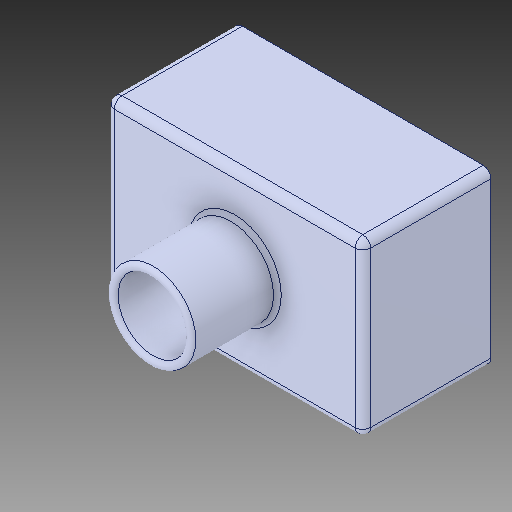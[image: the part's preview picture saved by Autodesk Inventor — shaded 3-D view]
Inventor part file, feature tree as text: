
AUTODESK INVENTOR PART (.ipt)
format: ipt  version: 2018 (Build 220112000, 112)  size: 159,232 bytes
history: native  units: in
note: dims shown in document units (in); Inventor stores cm internally (conversion verified against a paired STEP export)
features: fillet x1
ambient origin geometry x8: Origin, YZ Plane, XZ Plane, XY Plane, X Axis, Y Axis, Z Axis, Center Point
bodies: Solid1 (feature_tree)
feature tree (1):
  fillet  "Fillet10"  [1 undecoded]
note: 1 required parameter value undecoded (feature->parameter linkage not recoverable at this tier; creation-order binding heuristic only, values carry confidence <= 0.55)
